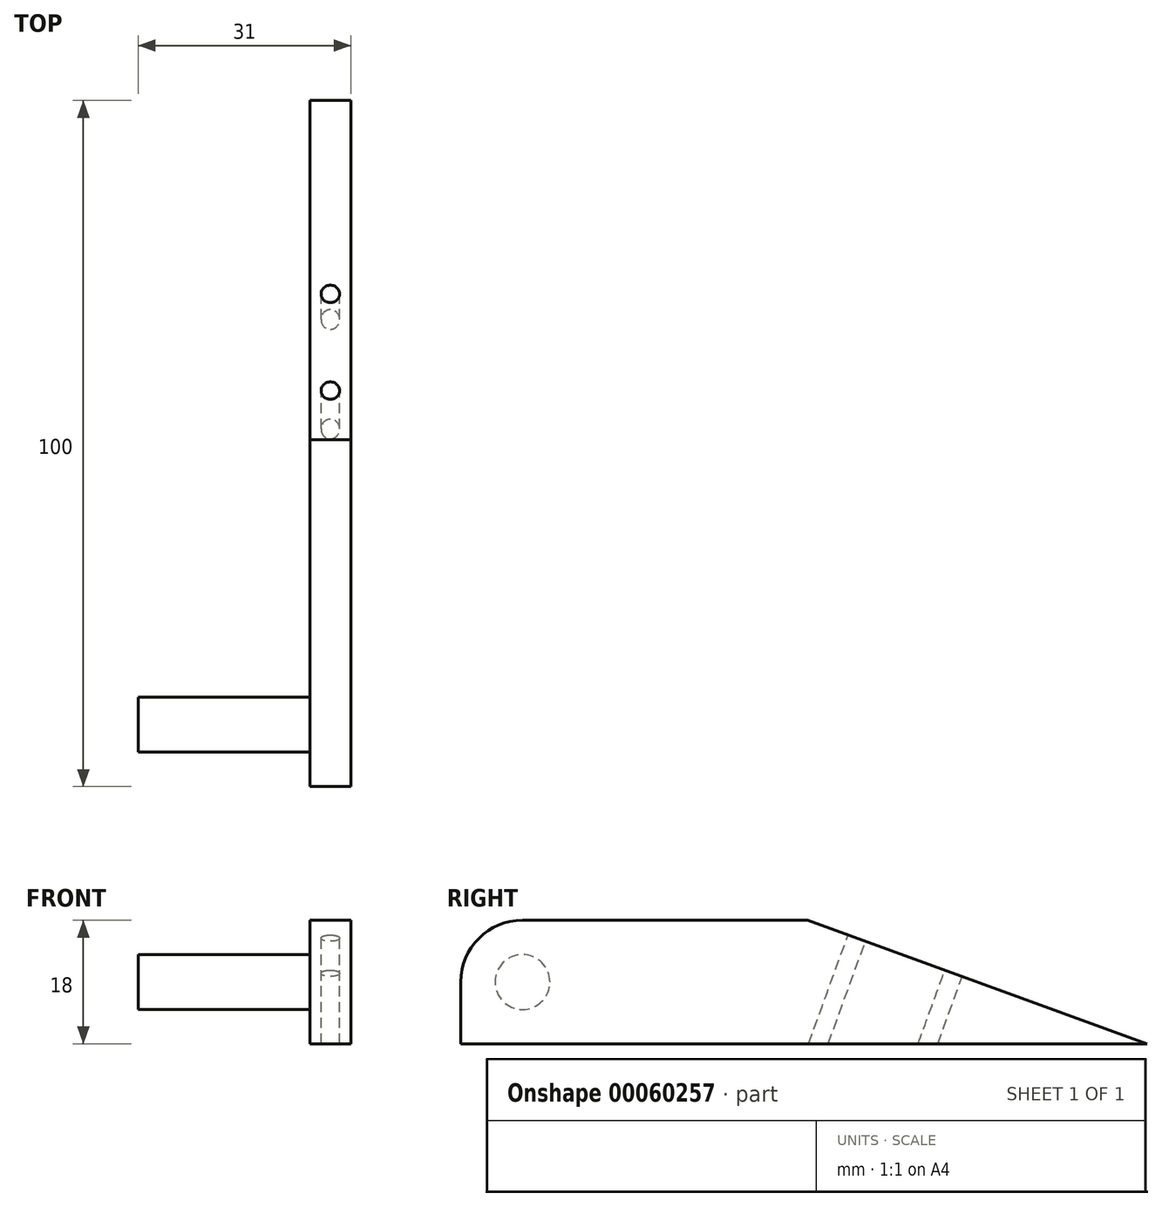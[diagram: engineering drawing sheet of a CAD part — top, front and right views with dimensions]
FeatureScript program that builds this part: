
annotation { "Feature Type Name" : "Feature", "Feature Type Description" : "" }
export const myFeature = defineFeature(function(context is Context, id is Id, definition is map)
    precondition{}
    {
        {
            var Q0;
            Q0=qCreatedBy(makeId("Right.planeOp"),FACE);
            var sketch = newSketch(context, id + "F0", { "sketchPlane" : qUnion([Q0])});
            skLineSegment(sketch, "E0", {"start": v(0, 0) * mm, "end": v(-49.45, 18) * mm});
            skLineSegment(sketch, "E1", {"start": v(-100, 0) * mm, "end": v(0, 0) * mm});
            skLineSegment(sketch, "E2", {"start": v(-49.45, 18) * mm, "end": v(-100, 18) * mm});
            skLineSegment(sketch, "E3", {"start": v(-100, 18) * mm, "end": v(-100, 0) * mm});
            skSolve(sketch);
        }
        {
            var Q0;
            Q0=qSketchRegion(id+"F0",true);
            extrude(context, id + "F1", {"entities" : qUnion([Q0]), "depth" : 6 * mm});
        }
        {
            var Q0;
            Q0=makeQuery(id+"F1.opExtrude","SWEPT_EDGE",EDGE,{"disambiguationData":[OSD([sQuery(id+"F0.wireOp",EDGE,"E2"),sQuery(id+"F0.wireOp",EDGE,"E3")])]});
            fillet(context, id + "F2", {"entities" : qUnion([Q0]), "radius" : 9 * mm, "tangentPropagation" : true, "allowEdgeOverflow" : false});
        }
        {
            var Q0;
            Q0=makeQuery(id+"F1.opExtrude","CAP_FACE",FACE,{"disambiguationData":[OSD([sQuery(id+"F0.wireOp",EDGE,"E0"),sQuery(id+"F0.wireOp",EDGE,"E1"),sQuery(id+"F0.wireOp",EDGE,"E2"),sQuery(id+"F0.wireOp",EDGE,"E3")])],"isStart":false});
            var sketch = newSketch(context, id + "F3", { "sketchPlane" : qUnion([Q0])});
            skCircle(sketch, "E4", {"center": v(-91, 9) * mm, "radius": 4 * mm});
            skSolve(sketch);
        }
        {
            var Q0;
            Q0=makeQuery(id+"F3.imprint","IMPRINT",FACE,{"disambiguationData":[TD([[makeQuery(id+"F3.imprint","IMPRINT",EDGE,{"derivedFrom":sQuery(id+"F3.wireOp",EDGE,"E4")}),1.0]])]});
            extrude(context, id + "F4", {"entities" : qUnion([Q0]), "operationType" : NewBodyOperationType.ADD, "depth" : 25 * mm});
        }
        {
            var Q0;
            Q0=makeQuery(id+"F1.opExtrude","SWEPT_BODY",BODY,{"disambiguationData":[OSD([sQuery(id+"F0.wireOp",EDGE,"E0"),sQuery(id+"F0.wireOp",EDGE,"E1"),sQuery(id+"F0.wireOp",EDGE,"E2"),sQuery(id+"F0.wireOp",EDGE,"E3"),sQuery(id+"F0.wireOp",EDGE,"X8ozzKDo-yYgY-9Q4E-a1CL-CWErJDXkymTs"),sQuery(id+"F0.wireOp",EDGE,"JyQerY5y-8dF4-qRYe-Bujd-8WPOWhhrlNX1")])]});
            var Q1;
            Q1=qCreatedBy(makeId("Right.planeOp"),FACE);
            mirror(context, id + "F5", {"entities" : qUnion([Q0]), "mirrorPlane" : qUnion([Q1])});
        }
        {
            var Q0;
            Q0=makeQuery(id+"F1.opExtrude","SWEPT_BODY",BODY,{"disambiguationData":[OSD([sQuery(id+"F0.wireOp",EDGE,"E0"),sQuery(id+"F0.wireOp",EDGE,"E1"),sQuery(id+"F0.wireOp",EDGE,"E2"),sQuery(id+"F0.wireOp",EDGE,"E3"),sQuery(id+"F0.wireOp",EDGE,"X8ozzKDo-yYgY-9Q4E-a1CL-CWErJDXkymTs"),sQuery(id+"F0.wireOp",EDGE,"JyQerY5y-8dF4-qRYe-Bujd-8WPOWhhrlNX1")])]});
            deleteBodies(context, id + "F6", {"entities" : qUnion([Q0])});
        }
        {
            var Q0;
            Q0=makeQuery(id+"F5.opPattern","COPY",FACE,{"derivedFrom":makeQuery(id+"F1.opExtrude","SWEPT_FACE",FACE,{"disambiguationData":[OSD([sQuery(id+"F0.wireOp",EDGE,"E0")])]}),"instanceName":"1"});
            var sketch = newSketch(context, id + "F7", { "sketchPlane" : qUnion([Q0])});
            skCircle(sketch, "E5", {"center": v(-3, -45) * mm, "radius": 1.35 * mm});
            skCircle(sketch, "E6", {"center": v(-3, -30) * mm, "radius": 1.35 * mm});
            skLineSegment(sketch, "E7", {"start": v(-3, -30) * mm, "end": v(0, -30) * mm, "construction": true});
            skLineSegment(sketch, "E8", {"start": v(-3, -30) * mm, "end": v(-6, -30) * mm, "construction": true});
            skSolve(sketch);
        }
        {
            var Q0;
            Q0 = qSketchRegion(id + "F7", true);
            extrude(context, id + "F8", {"entities" : qUnion([Q0]), "operationType" : NewBodyOperationType.REMOVE, "oppositeDirection" : true, "depth" : 25 * mm});
        }
    });
